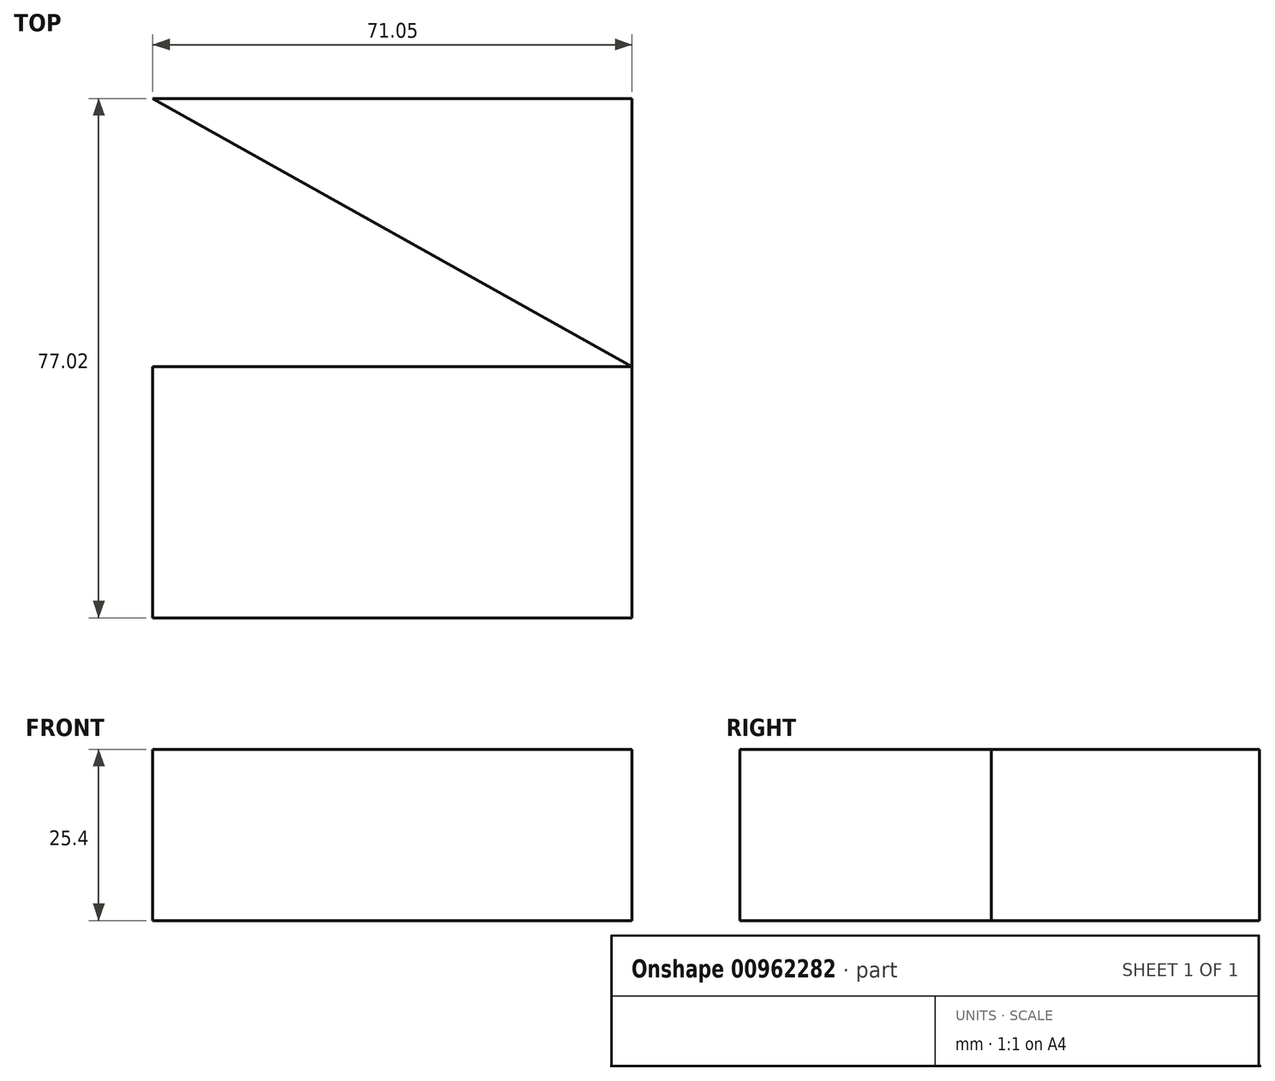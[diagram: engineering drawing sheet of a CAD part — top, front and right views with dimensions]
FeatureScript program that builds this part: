
annotation { "Feature Type Name" : "Feature", "Feature Type Description" : "" }
export const myFeature = defineFeature(function(context is Context, id is Id, definition is map)
    precondition{}
    {
        {
            var Q0;
            Q0=qCreatedBy(makeId("Top.planeOp"),FACE);
            var sketch = newSketch(context, id + "F0", { "sketchPlane" : qUnion([Q0])});
            skLineSegment(sketch, "E0", {"start": v(-40.63, -37.26) * mm, "end": v(30.42, -37.26) * mm});
            skLineSegment(sketch, "E1", {"start": v(30.42, -37.26) * mm, "end": v(30.42, 39.76) * mm});
            skLineSegment(sketch, "E2", {"start": v(30.42, 39.76) * mm, "end": v(-40.63, 39.76) * mm});
            skLineSegment(sketch, "E3", {"start": v(-40.63, 39.76) * mm, "end": v(30.42, 0) * mm});
            skLineSegment(sketch, "E4", {"start": v(30.42, 0) * mm, "end": v(-40.63, 0) * mm});
            skLineSegment(sketch, "E5", {"start": v(-40.63, 0) * mm, "end": v(-40.63, -37.26) * mm});
            skSolve(sketch);
        }
        {
            var Q0;
            Q0 = qSketchRegion(id + "F0", true);
            extrude(context, id + "F1", {"entities" : qUnion([Q0]), "depth" : 25.4 * mm, "offsetDistance" : 25.4 * mm});
        }
    });
